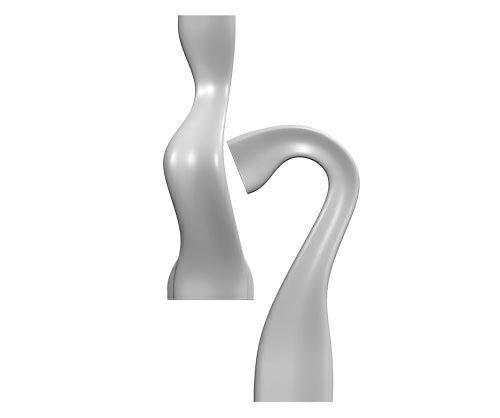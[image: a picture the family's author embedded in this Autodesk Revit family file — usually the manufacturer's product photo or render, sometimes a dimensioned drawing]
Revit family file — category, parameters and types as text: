
# Revit family: CITY ALPHABET litera „H”
name_source: partatom
category: Meble
revit_build: Autodesk Revit 2018 (Build: 20190510_1515(x64)
units: mm (PartAtom-declared; Revit-internal decimal feet)

## family parameters
Numer OmniClass = 23.40.10.11.14
Obiekt nadrzędny = Powierzchnia
Punkt obliczania pomieszczeń = Nie
Tnij formami wycięć po wczytaniu = Nie
Tytuł OmniClass = Exterior Seating
Współdzielony = Nie

## types (1)
- CITY ALPHABET litera „H”
    Domyślna rzędna = 1219 mm
    Długość = 3250 mm  [stored 10.6627 ft]
    IfcExportAs = IfcFurnishingElement
    Komentarze do typu = Ławka
    Materiał - informacja = Szeroki wybór kolorów wg palety RAL. Istnieje również możliwość specjalnego wykonania
kolorystycznego na indywidualne zapytanie klienta.
    Model = CITY ALPHABET litera „H”
    Obraz typu = H.jpg
    Producent = Astrini Design
    Szerokość = 1650 mm  [stored 5.41339 ft]
    Temepratura użytkowania = -40°C do 80°C, ( -40°F do 176°F )
    URL = http://astrini-design.pl
    Waga (szacunkowo) = 69.40 kg
    Waga po wypełnieniu (szacunkowo) = 169.00 kg
    Wysokość = 590 mm  [stored 1.9357 ft]

note: [stored X ft] marks values corroborated as IEEE doubles in the binary element streams (Revit-internal decimal feet)
